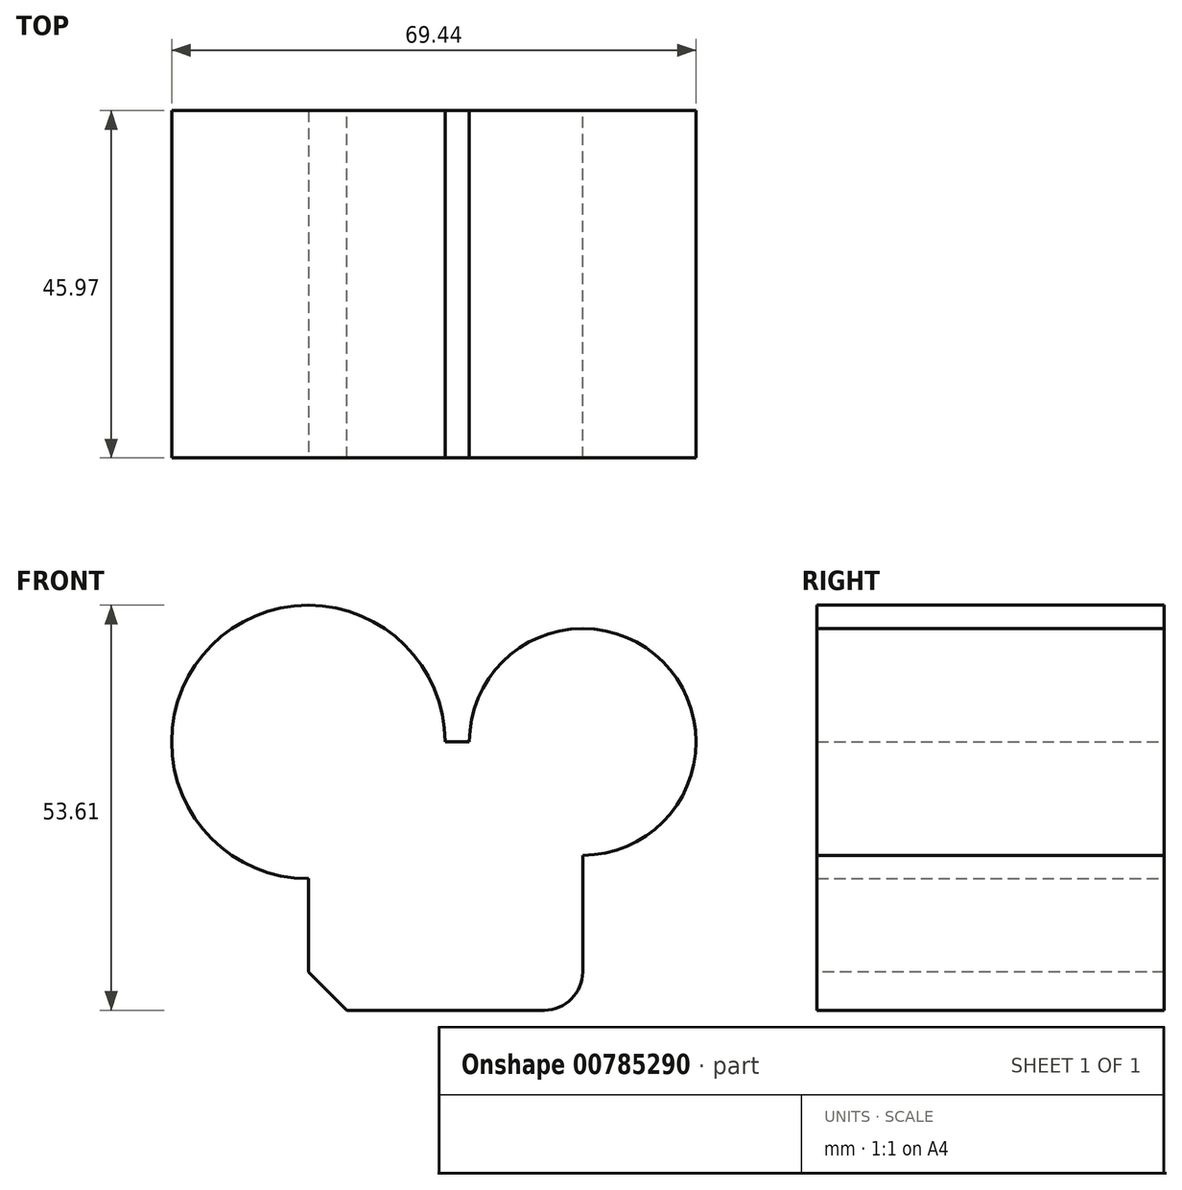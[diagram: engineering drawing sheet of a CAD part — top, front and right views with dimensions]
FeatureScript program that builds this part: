
annotation { "Feature Type Name" : "Feature", "Feature Type Description" : "" }
export const myFeature = defineFeature(function(context is Context, id is Id, definition is map)
    precondition{}
    {
        {
            var Q0;
            Q0=qCreatedBy(makeId("Front.planeOp"),FACE);
            var sketch = newSketch(context, id + "F0", { "sketchPlane" : qUnion([Q0])});
            skLineSegment(sketch, "E0", {"start": v(0, 0) * mm, "end": v(0, 17.42) * mm});
            skLineSegment(sketch, "E1", {"start": v(18.1, 35.51) * mm, "end": v(21.32, 35.51) * mm});
            skLineSegment(sketch, "E2", {"start": v(36.33, 20.5) * mm, "end": v(36.33, 0) * mm});
            skLineSegment(sketch, "E3", {"start": v(36.33, 0) * mm, "end": v(0, 0) * mm});
            skArc(sketch, "E4", {"start": v(18.1, 35.51) * mm, "mid": v(-12.8, 48.31) * mm, "end": v(0, 17.42) * mm});
            skArc(sketch, "E5", {"start": v(36.33, 20.5) * mm, "mid": v(46.94, 46.13) * mm, "end": v(21.32, 35.51) * mm});
            skSolve(sketch);
        }
        {
            var Q0;
            Q0 = qSketchRegion(id + "F0", true);
            extrude(context, id + "F1", {"entities" : qUnion([Q0]), "depth" : 45.97 * mm, "offsetDistance" : 25.4 * mm});
        }
        {
            var Q0;
            Q0=makeQuery(id+"F1.opExtrude","SWEPT_EDGE",EDGE,{"disambiguationData":[OSD([sQuery(id+"F0.wireOp",EDGE,"E0"),sQuery(id+"F0.wireOp",EDGE,"E3")])]});
            chamfer(context, id + "F2", {"entities" : qUnion([Q0]), "width" : 5.08 * mm, "tangentPropagation" : true});
        }
        {
            var Q0;
            Q0=makeQuery(id+"F1.opExtrude","SWEPT_EDGE",EDGE,{"disambiguationData":[OSD([sQuery(id+"F0.wireOp",EDGE,"E2"),sQuery(id+"F0.wireOp",EDGE,"E3")])]});
            fillet(context, id + "F3", {"entities" : qUnion([Q0]), "radius" : 5.08 * mm, "tangentPropagation" : true, "allowEdgeOverflow" : false});
        }
    });
